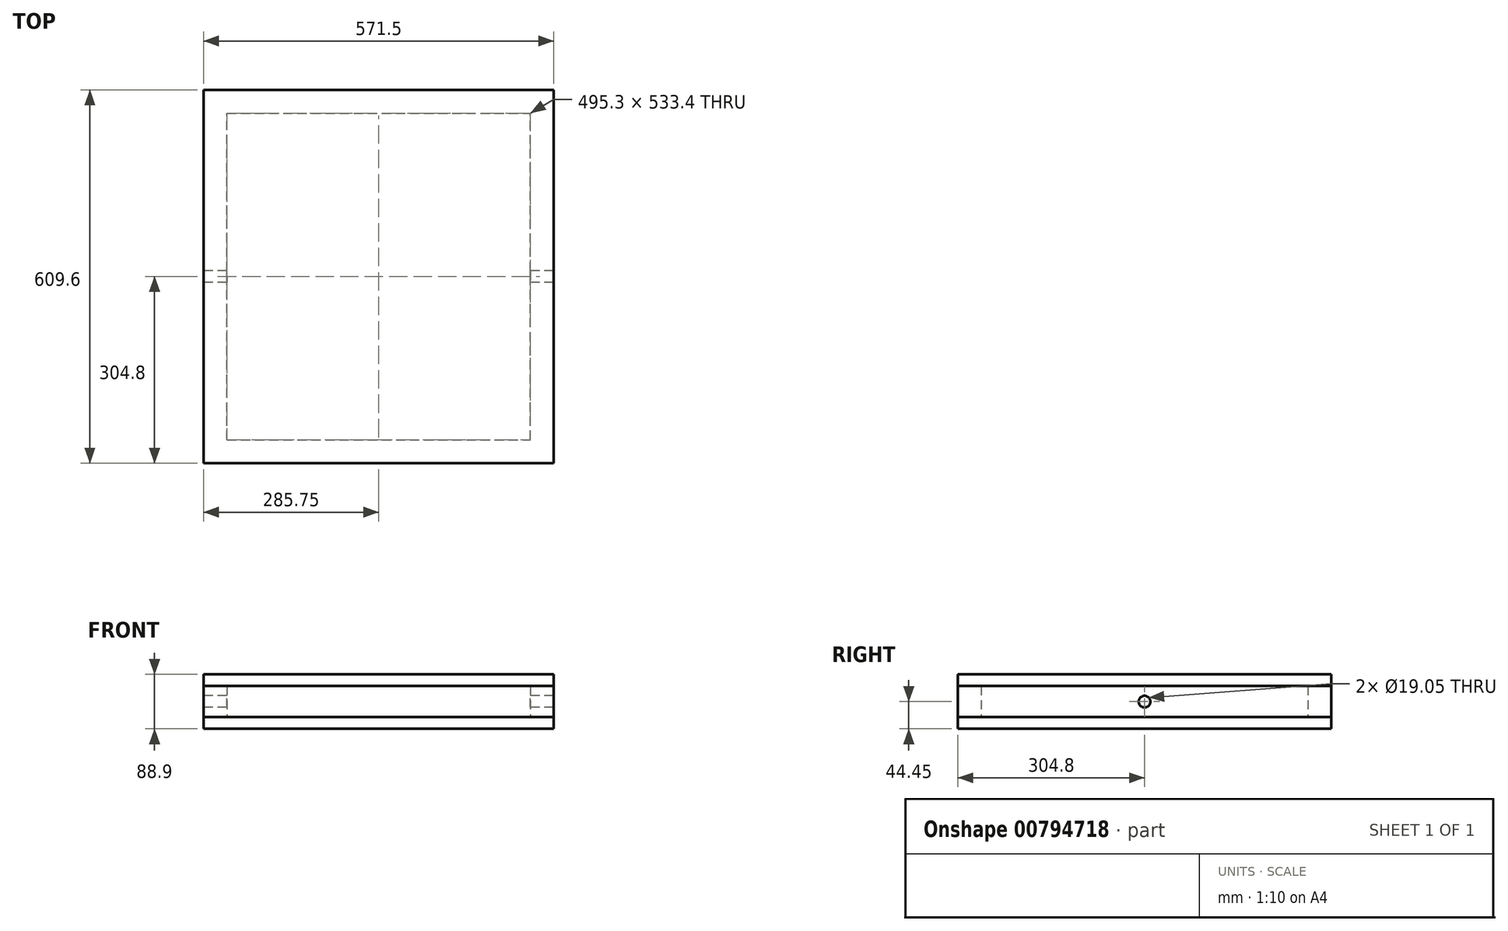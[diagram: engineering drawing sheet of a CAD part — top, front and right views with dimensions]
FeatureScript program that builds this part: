
annotation { "Feature Type Name" : "Feature", "Feature Type Description" : "" }
export const myFeature = defineFeature(function(context is Context, id is Id, definition is map)
    precondition{}
    {
        {
            var Q0;
            Q0=qCreatedBy(makeId("Front.planeOp"),FACE);
            var sketch = newSketch(context, id + "F0", { "sketchPlane" : qUnion([Q0])});
            skLineSegment(sketch, "E0.bottom", {"start": v(-285.75, 25.4) * mm, "end": v(285.75, 25.4) * mm});
            skLineSegment(sketch, "E0.top", {"start": v(-285.75, -25.4) * mm, "end": v(285.75, -25.4) * mm});
            skLineSegment(sketch, "E0.left", {"start": v(-285.75, 25.4) * mm, "end": v(-285.75, -25.4) * mm});
            skLineSegment(sketch, "E0.right", {"start": v(285.75, 25.4) * mm, "end": v(285.75, -25.4) * mm});
            skPoint(sketch, "E0.middle", {"position": v(0, 0) * mm});
            skSolve(sketch);
        }
        {
            var Q0;
            Q0=makeQuery(id+"F0.imprint","IMPRINT",FACE,{"disambiguationData":[TD([[makeQuery(id+"F0.imprint","IMPRINT",EDGE,{"derivedFrom":sQuery(id+"F0.wireOp",EDGE,"E0.bottom")}),-1.0]])]});
            extrude(context, id + "F1", {"entities" : qUnion([Q0]), "depth" : 609.6 * mm, "offsetDistance" : 25.4 * mm});
        }
        {
            var Q0;
            Q0=makeQuery(id+"F1.opExtrude","SWEPT_FACE",FACE,{"disambiguationData":[OSD([sQuery(id+"F0.wireOp",EDGE,"E0.left")])]});
            var sketch = newSketch(context, id + "F2", { "sketchPlane" : qUnion([Q0])});
            skCircle(sketch, "E1", {"center": v(304.8, 0) * mm, "radius": 9.53 * mm});
            skPoint(sketch, "E1.centerSnap0", {"position": v(304.8, -25.4) * mm});
            skPoint(sketch, "E1.centerSnap1", {"position": v(0, 0) * mm});
            skSolve(sketch);
        }
        {
            var Q0;
            Q0=makeQuery(id+"F2.imprint","IMPRINT",FACE,{"disambiguationData":[TD([[makeQuery(id+"F2.imprint","IMPRINT",EDGE,{"derivedFrom":sQuery(id+"F2.wireOp",EDGE,"E1")}),1.0]])]});
            extrude(context, id + "F3", {"entities" : qUnion([Q0]), "operationType" : NewBodyOperationType.REMOVE, "endBound" : BoundingType.THROUGH_ALL, "oppositeDirection" : true, "depth" : 25.4 * mm, "offsetDistance" : 25.4 * mm});
        }
        {
            var Q0;
            Q0=makeQuery(id+"F1.opExtrude","SWEPT_FACE",FACE,{"disambiguationData":[OSD([sQuery(id+"F0.wireOp",EDGE,"E0.top")])]});
            var sketch = newSketch(context, id + "F4", { "sketchPlane" : qUnion([Q0])});
            skLineSegment(sketch, "E2.bottom", {"start": v(247.65, 38.1) * mm, "end": v(-247.65, 38.1) * mm});
            skLineSegment(sketch, "E2.top", {"start": v(247.65, 571.5) * mm, "end": v(-247.65, 571.5) * mm});
            skLineSegment(sketch, "E2.left", {"start": v(247.65, 38.1) * mm, "end": v(247.65, 571.5) * mm});
            skLineSegment(sketch, "E2.right", {"start": v(-247.65, 38.1) * mm, "end": v(-247.65, 571.5) * mm});
            skPoint(sketch, "E2.middle", {"position": v(0, 304.8) * mm});
            skPoint(sketch, "E2.middle.positionSnap0", {"position": v(-285.75, 304.8) * mm});
            skPoint(sketch, "E2.middle.positionSnap1", {"position": v(0, 609.6) * mm});
            skPoint(sketch, "E2.centerSnap0", {"position": v(-285.75, 304.8) * mm});
            skPoint(sketch, "E2.centerSnap1", {"position": v(0, 609.6) * mm});
            skSolve(sketch);
        }
        {
            var Q0;
            Q0=makeQuery(id+"F4.imprint","IMPRINT",FACE,{"disambiguationData":[TD([[makeQuery(id+"F4.imprint","IMPRINT",EDGE,{"derivedFrom":sQuery(id+"F4.wireOp",EDGE,"E2.bottom")}),-1.0]])]});
            extrude(context, id + "F5", {"entities" : qUnion([Q0]), "operationType" : NewBodyOperationType.REMOVE, "endBound" : BoundingType.THROUGH_ALL, "oppositeDirection" : true, "depth" : 25.4 * mm, "offsetDistance" : 25.4 * mm});
        }
        {
            var Q0;
            Q0=makeQuery(id+"F1.opExtrude","SWEPT_FACE",FACE,{"disambiguationData":[OSD([sQuery(id+"F0.wireOp",EDGE,"E0.bottom")])]});
            var sketch = newSketch(context, id + "F6", { "sketchPlane" : qUnion([Q0])});
            skLineSegment(sketch, "E3.bottom", {"start": v(285.75, -609.6) * mm, "end": v(-285.75, -609.6) * mm});
            skLineSegment(sketch, "E3.top", {"start": v(285.75, 0) * mm, "end": v(-285.75, 0) * mm});
            skLineSegment(sketch, "E3.left", {"start": v(285.75, -609.6) * mm, "end": v(285.75, 0) * mm});
            skLineSegment(sketch, "E3.right", {"start": v(-285.75, -609.6) * mm, "end": v(-285.75, 0) * mm});
            skPoint(sketch, "E3.middle", {"position": v(0, -304.8) * mm});
            skPoint(sketch, "E3.middle.positionSnap0", {"position": v(247.65, -304.8) * mm});
            skPoint(sketch, "E3.centerSnap0", {"position": v(247.65, -304.8) * mm});
            skSolve(sketch);
        }
        {
            var Q0;
            Q0 = qSketchRegion(id + "F6", true);
            extrude(context, id + "F7", {"entities" : qUnion([Q0]), "depth" : 19.05 * mm, "offsetDistance" : 25.4 * mm});
        }
        {
            var Q0;
            Q0=makeQuery(id+"F7.opExtrude","SWEPT_BODY",BODY,{"disambiguationData":[OSD([sQuery(id+"F6.wireOp",EDGE,"E3.bottom"),sQuery(id+"F6.wireOp",EDGE,"E3.top"),sQuery(id+"F6.wireOp",EDGE,"E3.left"),sQuery(id+"F6.wireOp",EDGE,"E3.right")])]});
            var Q1;
            Q1=qCreatedBy(makeId("Top.planeOp"),FACE);
            mirror(context, id + "F8", {"entities" : qUnion([Q0]), "mirrorPlane" : qUnion([Q1])});
        }
    });
